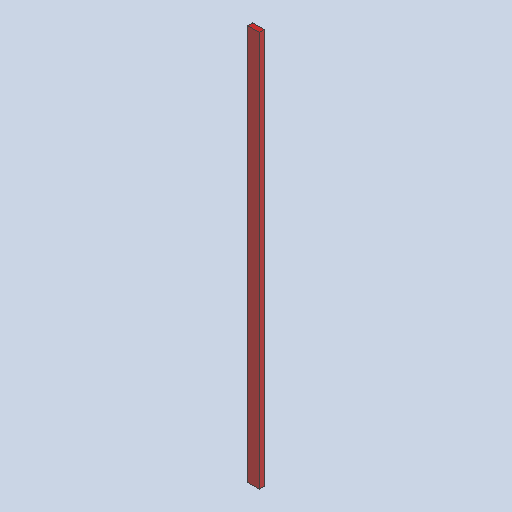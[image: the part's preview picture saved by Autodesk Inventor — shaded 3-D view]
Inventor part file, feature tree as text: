
AUTODESK INVENTOR PART (.ipt)
format: ipt  version: 2025 (Build 290162000, 162)  size: 259,584 bytes
history: native  units: in
note: dims shown in document units (in); Inventor stores cm internally (conversion verified against a paired STEP export)
features: extrude x1, sketch x1, other x1
ambient origin geometry x8: Origin, YZ Plane, XZ Plane, XY Plane, X Axis, Y Axis, Z Axis, Center Point
bodies: Solid1 (feature_tree)
feature tree (3):
  extrude  "Extrusion1"  Depth=3.5in
  sketch  "Sketch1"  dims[d0=1.5in d1=3.5in d2=120.0in d3=0.0in]
  other  "Finish1"
